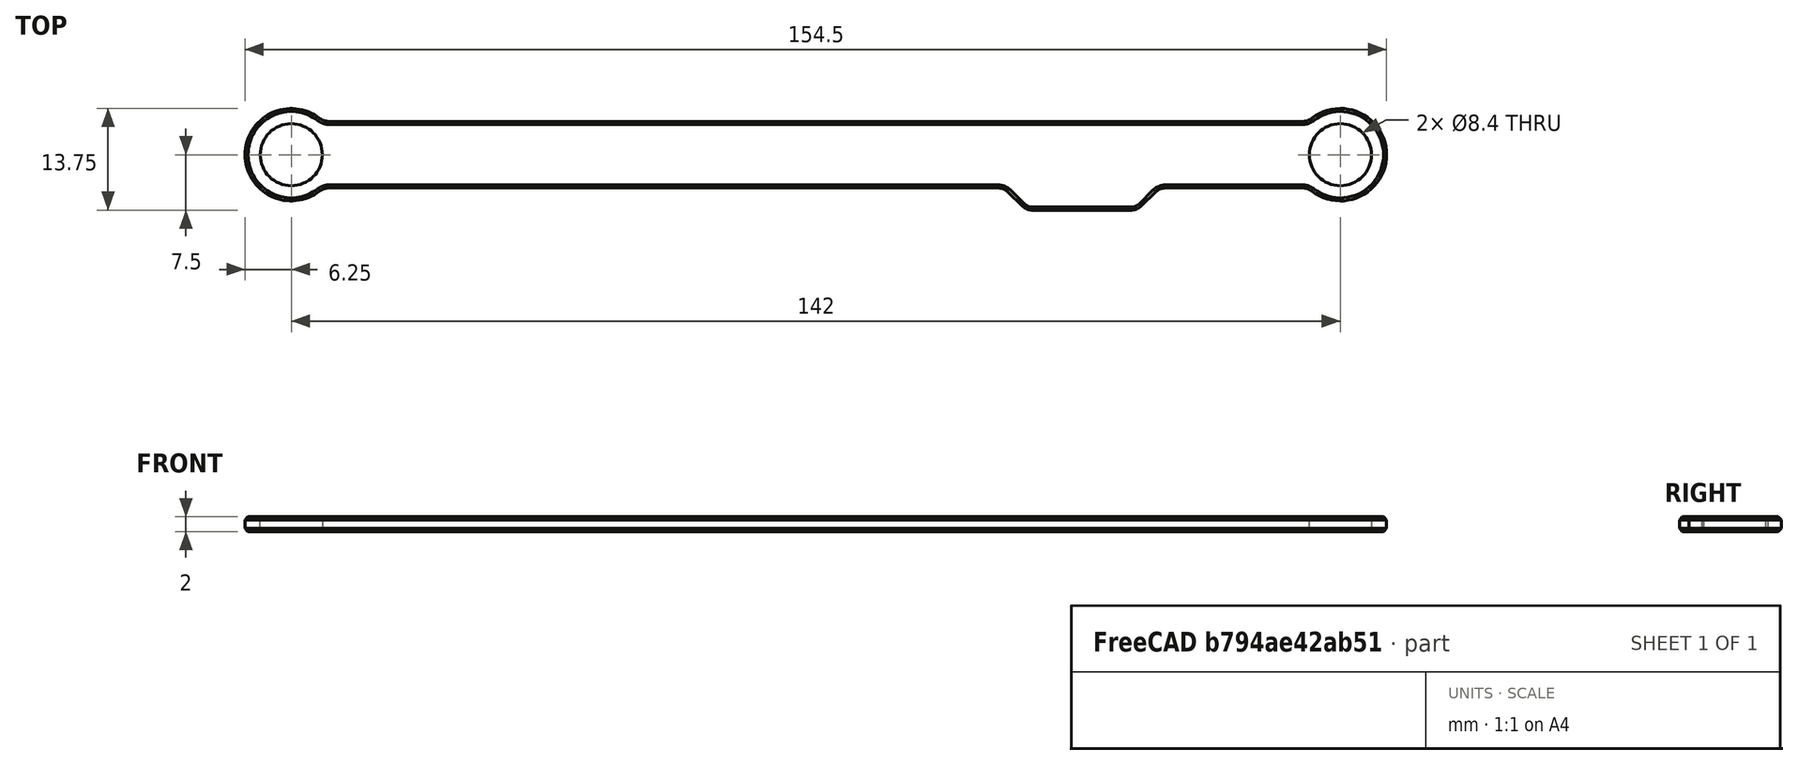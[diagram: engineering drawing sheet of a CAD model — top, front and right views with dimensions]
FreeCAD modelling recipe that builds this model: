
FCSTD DOCUMENT  (FreeCAD 0.18R16146 (Git))
Label: ResizedLeftChainAuxiliaryRod
License: All rights reserved
LicenseURL: http://en.wikipedia.org/wiki/All_rights_reserved
objects: Part::Feature×1, PartDesign::FeatureBase×1, Sketcher::SketchObject×1, PartDesign::Pocket×1, PartDesign::Body×1
note: 6 computed .brp shape members not serialized (recipe doc carries the construction recipe); baked Part::Feature solids carry a one-line shape summary decoded from their .brp

FEATURE [Part::Feature] Part__Feature001  label="س²ၬ¸ɀ"
  Placement = pos=(126.597,220.933,-104.204) rot=(0.80045,0.5994,0;3.14159rad)
  shape: bbox 52.46 x 148.8 x 2 mm, 57 faces (baked)
FEATURE [PartDesign::FeatureBase] BaseFeature
  BaseFeature = -> Part__Feature001
FEATURE [Sketcher::SketchObject] Sketch
  ExternalGeometry = -> [BaseFeature]
  MapMode = 5
  Placement = pos=(0,0,1) rot=(0,0,1;0rad)
  Support = -> [BaseFeature]
  sketch-geometry (2):
    g0: Circle CenterX=-71 CenterY=0 CenterZ=0 NormalX=0 NormalY=0 NormalZ=1 AngleXU=0 Radius=4.2
    g1: Circle CenterX=71 CenterY=0 CenterZ=0 NormalX=0 NormalY=0 NormalZ=1 AngleXU=0 Radius=4.2
  constraints (4):
    c: Radius(g0) = 4.2
    c: Coincident(g0,g-4)
    c: Coincident(g1,g-6)
    c: Radius(g1) = 4.2
FEATURE [PartDesign::Pocket] Pocket
  BaseFeature = -> BaseFeature
  Length = 5
  Length2 = 100
  Profile = -> Sketch
  Type = 1
FEATURE [PartDesign::Body] Body  label="ResizedLeftChainAuxiliaryRod"
  BaseFeature = -> Part__Feature001
  Group = -> [BaseFeature,Sketch,Pocket]
  Origin = -> Origin
  Tip = -> Pocket
